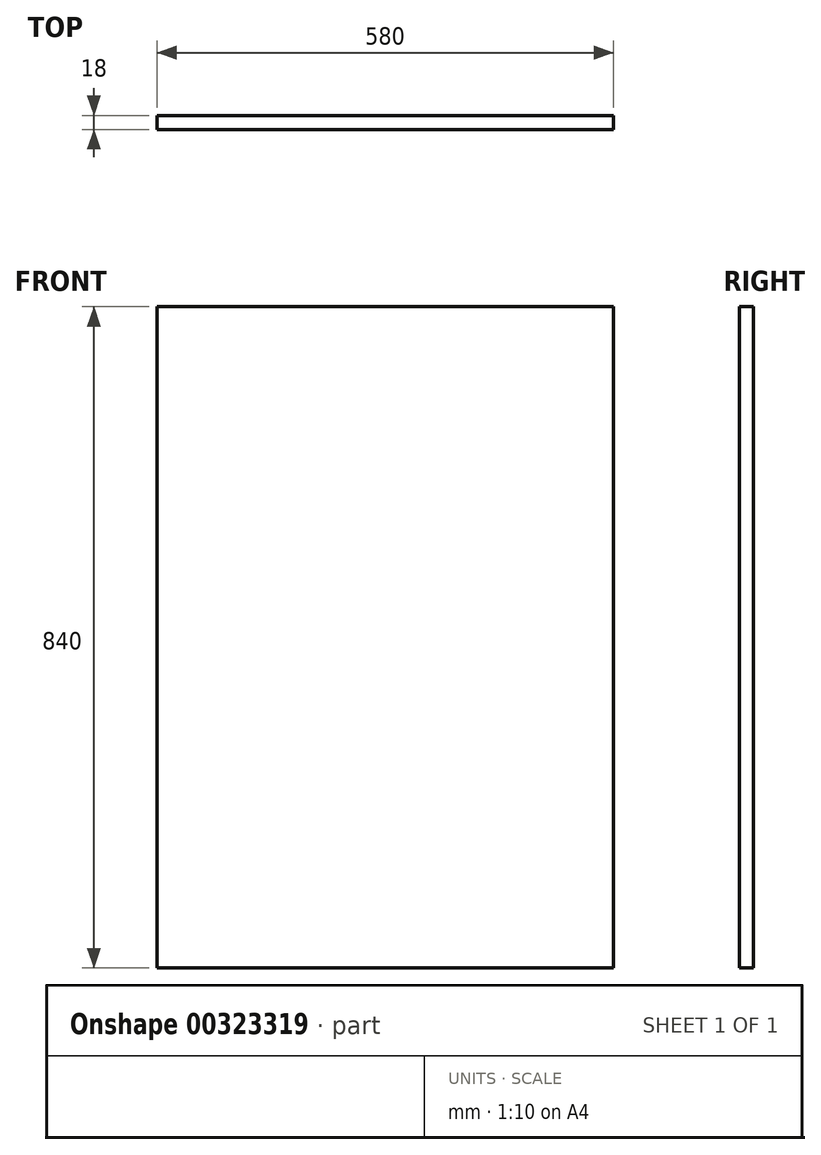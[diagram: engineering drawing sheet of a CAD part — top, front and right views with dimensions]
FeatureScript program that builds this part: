
annotation { "Feature Type Name" : "Feature", "Feature Type Description" : "" }
export const myFeature = defineFeature(function(context is Context, id is Id, definition is map)
    precondition{}
    {
        {
            var Q0;
            Q0=qCreatedBy(makeId("Front.planeOp"),FACE);
            var sketch = newSketch(context, id + "F0", { "sketchPlane" : qUnion([Q0])});
            skLineSegment(sketch, "E0.bottom", {"start": v(0, 0) * mm, "end": v(580, 0) * mm});
            skLineSegment(sketch, "E0.top", {"start": v(0, 840) * mm, "end": v(580, 840) * mm});
            skLineSegment(sketch, "E0.left", {"start": v(0, 0) * mm, "end": v(0, 840) * mm});
            skLineSegment(sketch, "E0.right", {"start": v(580, 0) * mm, "end": v(580, 840) * mm});
            skSolve(sketch);
        }
        {
            var Q0;
            Q0 = qSketchRegion(id + "F0", true);
            extrude(context, id + "F1", {"entities" : qUnion([Q0]), "depth" : 18 * mm});
        }
    });
